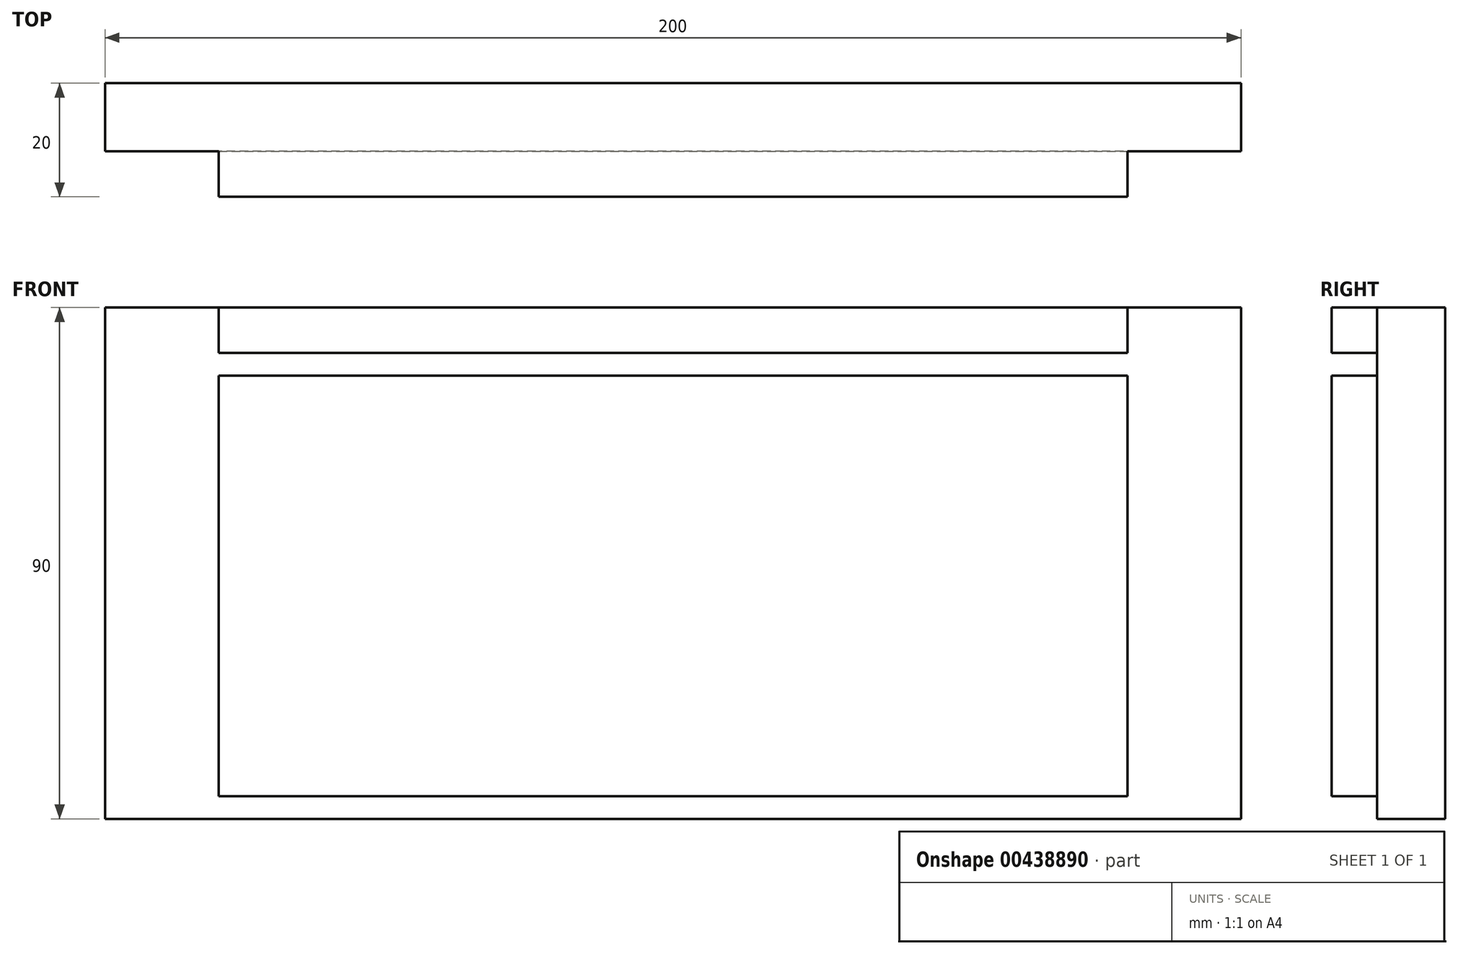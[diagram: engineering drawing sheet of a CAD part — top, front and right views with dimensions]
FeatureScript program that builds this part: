
annotation { "Feature Type Name" : "Feature", "Feature Type Description" : "" }
export const myFeature = defineFeature(function(context is Context, id is Id, definition is map)
    precondition{}
    {
        {
            var Q0;
            Q0=qCreatedBy(makeId("Front.planeOp"),FACE);
            var sketch = newSketch(context, id + "F0", { "sketchPlane" : qUnion([Q0])});
            skLineSegment(sketch, "E0.bottom", {"start": v(100, 45) * mm, "end": v(-100, 45) * mm});
            skLineSegment(sketch, "E0.top", {"start": v(100, -45) * mm, "end": v(-100, -45) * mm});
            skLineSegment(sketch, "E0.left", {"start": v(100, 45) * mm, "end": v(100, -45) * mm});
            skLineSegment(sketch, "E0.right", {"start": v(-100, 45) * mm, "end": v(-100, -45) * mm});
            skPoint(sketch, "E0.middle", {"position": v(0, 0) * mm});
            skLineSegment(sketch, "E1", {"start": v(-80, 45) * mm, "end": v(-80, -45) * mm});
            skLineSegment(sketch, "E2", {"start": v(80, 45) * mm, "end": v(80, -45) * mm});
            skLineSegment(sketch, "E3", {"start": v(-80, 37) * mm, "end": v(80, 37) * mm});
            skLineSegment(sketch, "E4", {"start": v(-80, 33) * mm, "end": v(80, 33) * mm});
            skLineSegment(sketch, "E5", {"start": v(-80, -41) * mm, "end": v(80, -41) * mm});
            skSolve(sketch);
        }
        {
            var Q0;
            {var subQ5=sQuery(id+"F0.wireOp",EDGE,"E5");Q0=makeQuery(id+"F0.imprint","IMPRINT",FACE,{"disambiguationData":[TD([[makeQuery(id+"F0.imprint","IMPRINT",EDGE,{"derivedFrom":subQ5}),-1.0]])]});}
            var Q1;
            {var subQ4=sQuery(id+"F0.wireOp",EDGE,"E0.left");Q1=makeQuery(id+"F0.imprint","IMPRINT",FACE,{"disambiguationData":[TD([[makeQuery(id+"F0.imprint","IMPRINT",EDGE,{"derivedFrom":subQ4}),-1.0]])]});}
            var Q2;
            {var subQ4=sQuery(id+"F0.wireOp",EDGE,"E0.right");Q2=makeQuery(id+"F0.imprint","IMPRINT",FACE,{"disambiguationData":[TD([[makeQuery(id+"F0.imprint","IMPRINT",EDGE,{"derivedFrom":subQ4}),1.0]])]});}
            var Q3;
            {var subQ0=sQuery(id+"F0.wireOp",EDGE,"E3");Q3=makeQuery(id+"F0.imprint","IMPRINT",FACE,{"disambiguationData":[TD([[makeQuery(id+"F0.imprint","IMPRINT",EDGE,{"derivedFrom":subQ0}),-1.0]])]});}
            extrude(context, id + "F1", {"entities" : qUnion([Q0, Q1, Q2, Q3]), "depth" : 12 * mm});
        }
        {
            var Q0;
            {var subQ5=sQuery(id+"F0.wireOp",EDGE,"E3");Q0=makeQuery(id+"F0.imprint","IMPRINT",FACE,{"disambiguationData":[TD([[makeQuery(id+"F0.imprint","IMPRINT",EDGE,{"derivedFrom":subQ5}),1.0]])]});}
            var Q1;
            {var subQ0=sQuery(id+"F0.wireOp",EDGE,"E4");Q1=makeQuery(id+"F0.imprint","IMPRINT",FACE,{"disambiguationData":[TD([[makeQuery(id+"F0.imprint","IMPRINT",EDGE,{"derivedFrom":subQ0}),-1.0]])]});}
            extrude(context, id + "F2", {"entities" : qUnion([Q0, Q1]), "operationType" : NewBodyOperationType.ADD, "depth" : 20 * mm});
        }
    });
